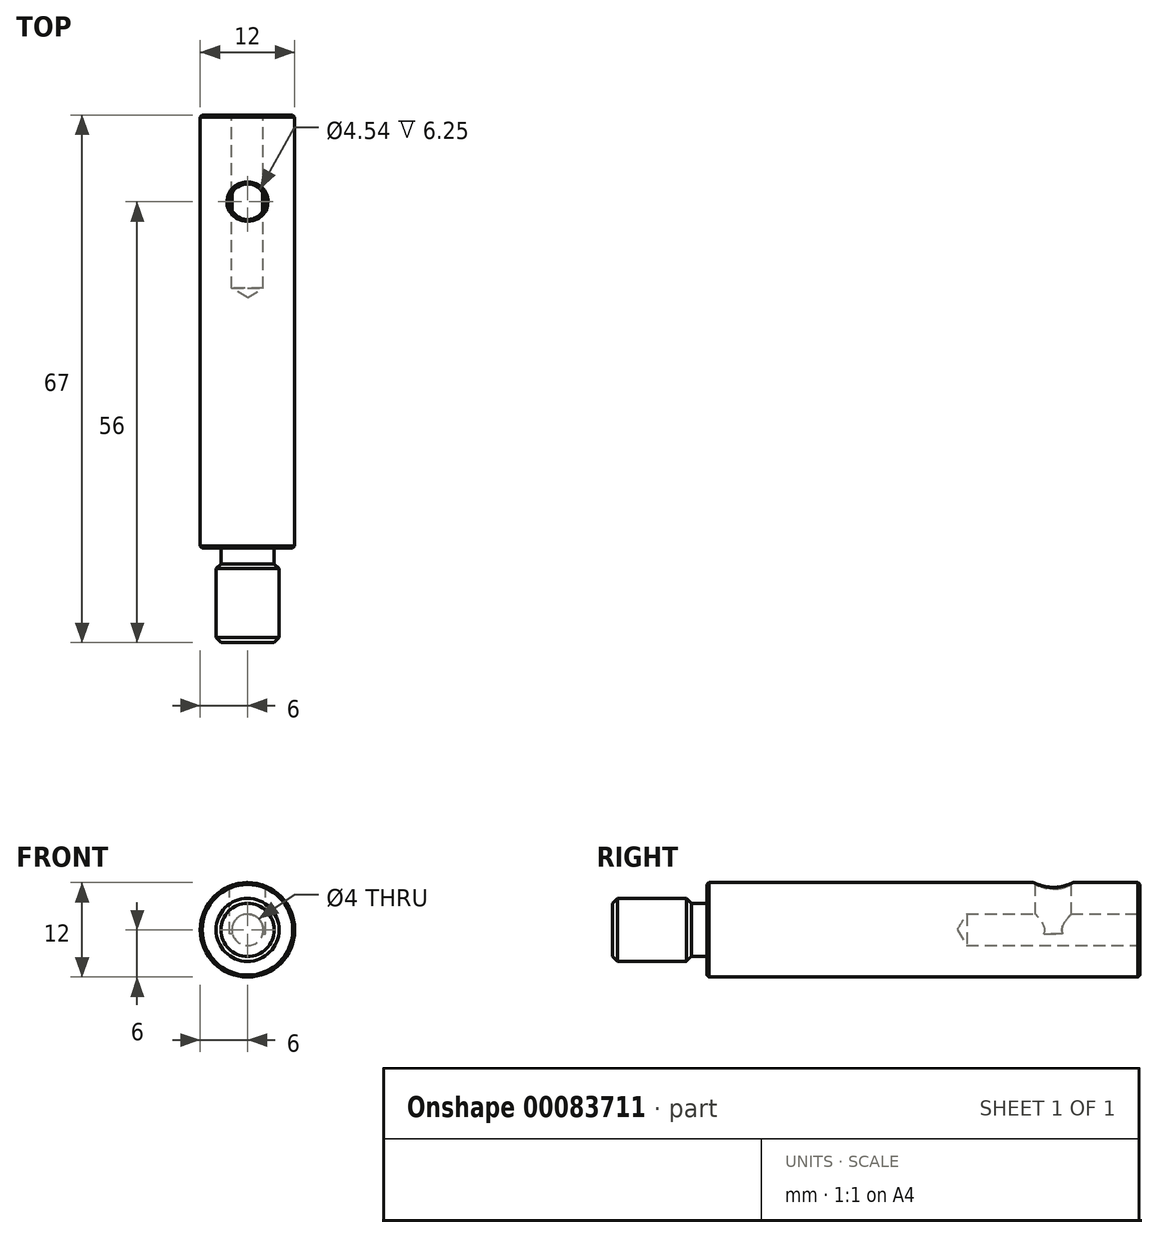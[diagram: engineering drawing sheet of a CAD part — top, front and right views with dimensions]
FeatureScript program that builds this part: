
annotation { "Feature Type Name" : "Feature", "Feature Type Description" : "" }
export const myFeature = defineFeature(function(context is Context, id is Id, definition is map)
    precondition{}
    {
        {
            var Q0;
            Q0=qCreatedBy(makeId("Front.planeOp"),FACE);
            var sketch = newSketch(context, id + "F0", { "sketchPlane" : qUnion([Q0])});
            skCircle(sketch, "E0", {"center": v(0, 0) * mm, "radius": 6 * mm});
            skSolve(sketch);
        }
        {
            var Q0;
            Q0=qSketchRegion(id+"F0",true);
            extrude(context, id + "F1", {"entities" : qUnion([Q0]), "depth" : 55 * mm});
        }
        {
            var Q0;
            Q0=makeQuery(id+"F1.opExtrude","CAP_FACE",FACE,{"disambiguationData":[OSD([sQuery(id+"F0.wireOp",EDGE,"E0")])],"isStart":false});
            var sketch = newSketch(context, id + "F2", { "sketchPlane" : qUnion([Q0])});
            skCircle(sketch, "E1", {"center": v(0, 0) * mm, "radius": 3.38 * mm});
            skSolve(sketch);
        }
        {
            var Q0;
            Q0=qSketchRegion(id+"F2",true);
            extrude(context, id + "F3", {"entities" : qUnion([Q0]), "operationType" : NewBodyOperationType.ADD, "depth" : 2 * mm});
        }
        {
            var Q0;
            Q0=makeQuery(id+"F3.opExtrude","CAP_FACE",FACE,{"disambiguationData":[OSD([sQuery(id+"F2.wireOp",EDGE,"E1")])],"isStart":false});
            var sketch = newSketch(context, id + "F4", { "sketchPlane" : qUnion([Q0])});
            skCircle(sketch, "E2", {"center": v(0, 0) * mm, "radius": 4 * mm});
            skSolve(sketch);
        }
        {
            var Q0;
            Q0=qSketchRegion(id+"F4",true);
            extrude(context, id + "F5", {"entities" : qUnion([Q0]), "operationType" : NewBodyOperationType.ADD, "depth" : 10 * mm});
        }
        {
            var Q0;
            Q0=makeQuery(id+"F5.opExtrude","SWEPT_FACE",FACE,{"disambiguationData":[OSD([sQuery(id+"F4.wireOp",EDGE,"E2")])]});
            chamfer(context, id + "F6", {"entities" : qUnion([Q0]), "width" : .625 * mm, "tangentPropagation" : true});
        }
        {
            var Q0;
            Q0=makeQuery(id+"F1.opExtrude","CAP_FACE",FACE,{"disambiguationData":[OSD([sQuery(id+"F0.wireOp",EDGE,"E0")])],"isStart":true});
            var sketch = newSketch(context, id + "F7", { "sketchPlane" : qUnion([Q0])});
            skPoint(sketch, "E3", {"position": v(0, 0) * mm});
            skSolve(sketch);
        }
        {
            var Q0;
            Q0=sQuery(id+"F7.wireOp",VERTEX,"E3");
            var Q1;
            Q1=makeQuery(id+"F1.opExtrude","SWEPT_BODY",BODY,{"disambiguationData":[OSD([sQuery(id+"F0.wireOp",EDGE,"E0")])]});
            hole(context, id + "F8", {"style" : HoleStyle.SIMPLE, "holeDiameter" : 4 * mm, "endStyle" : HoleEndStyle.BLIND, "holeDepth" : 22 * mm, "locations" : qUnion([Q0]), "scope" : qUnion([Q1])});
        }
        {
            var Q0;
            Q0=qCreatedBy(makeId("Top.planeOp"),FACE);
            cPlane(context, id + "F9", {"entities" : qUnion([Q0]), "cplaneType" : CPlaneType.OFFSET, "offset" : 6 * mm, "width" : 150 * mm, "height" : 150 * mm});
        }
        {
            var Q0;
            Q0=qCreatedBy(id+"F9.planeOp",FACE);
            var sketch = newSketch(context, id + "F10", { "sketchPlane" : qUnion([Q0])});
            skCircle(sketch, "E4", {"center": v(0, -11) * mm, "radius": 2.27 * mm});
            skSolve(sketch);
        }
        {
            var Q0;
            Q0=qSketchRegion(id+"F10",true);
            extrude(context, id + "F11", {"entities" : qUnion([Q0]), "operationType" : NewBodyOperationType.REMOVE, "oppositeDirection" : true, "depth" : 6.5 * mm});
        }
        {
            var Q0;
            Q0=makeQuery(id+"F1.opExtrude","SWEPT_FACE",FACE,{"disambiguationData":[OSD([sQuery(id+"F0.wireOp",EDGE,"E0")])]});
            chamfer(context, id + "F12", {"entities" : qUnion([Q0]), "width" : .25 * mm, "tangentPropagation" : true});
        }
    });
